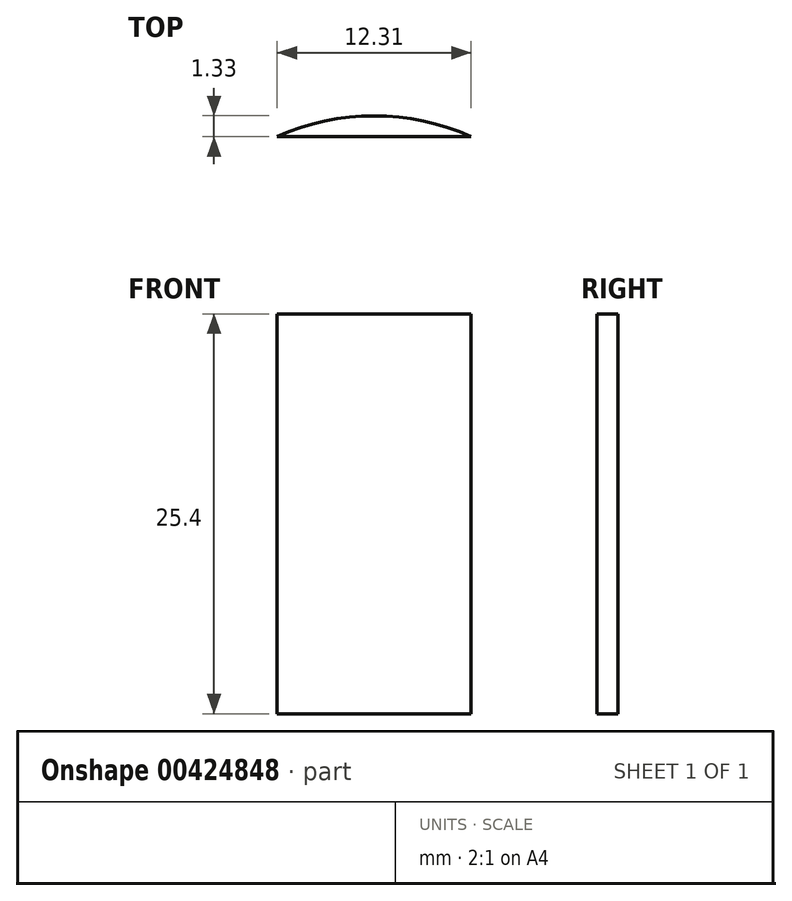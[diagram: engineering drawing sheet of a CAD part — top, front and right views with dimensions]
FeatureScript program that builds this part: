
annotation { "Feature Type Name" : "Feature", "Feature Type Description" : "" }
export const myFeature = defineFeature(function(context is Context, id is Id, definition is map)
    precondition{}
    {
        {
            var Q0;
            Q0=qCreatedBy(makeId("Top.planeOp"),FACE);
            var sketch = newSketch(context, id + "F0", { "sketchPlane" : qUnion([Q0])});
            skLineSegment(sketch, "E0.bottom", {"start": v(-38.61, 29.87) * mm, "end": v(28.82, 29.87) * mm});
            skLineSegment(sketch, "E0.top", {"start": v(-38.61, 0) * mm, "end": v(28.82, 0) * mm});
            skLineSegment(sketch, "E0.left", {"start": v(-38.61, 29.87) * mm, "end": v(-38.61, 0) * mm});
            skLineSegment(sketch, "E0.right", {"start": v(28.82, 29.87) * mm, "end": v(28.82, 0) * mm});
            skCircle(sketch, "E1", {"center": v(-7.68, 16.23) * mm, "radius": 14.96 * mm});
            skSolve(sketch);
        }
        {
            var Q0;
            {var subQ0=sQuery(id+"F0.wireOp",EDGE,"E1");var subQ1=sQuery(id+"F0.wireOp",EDGE,"E0.bottom");var subQ2=makeQuery(id+"F0.imprint","INTERSECT",VERTEX,{"disambiguationData":[OD(0.0)],"derivedFrom":[subQ1,subQ0]});Q0=makeQuery(id+"F0.imprint","IMPRINT",FACE,{"disambiguationData":[TD([[makeQuery(id+"F0.imprint","IMPRINT",EDGE,{"disambiguationData":[TD([[subQ2,-1.0]])],"derivedFrom":subQ1}),1.0]])]});}
            extrude(context, id + "F1", {"entities" : qUnion([Q0]), "depth" : 25.4 * mm});
        }
    });
